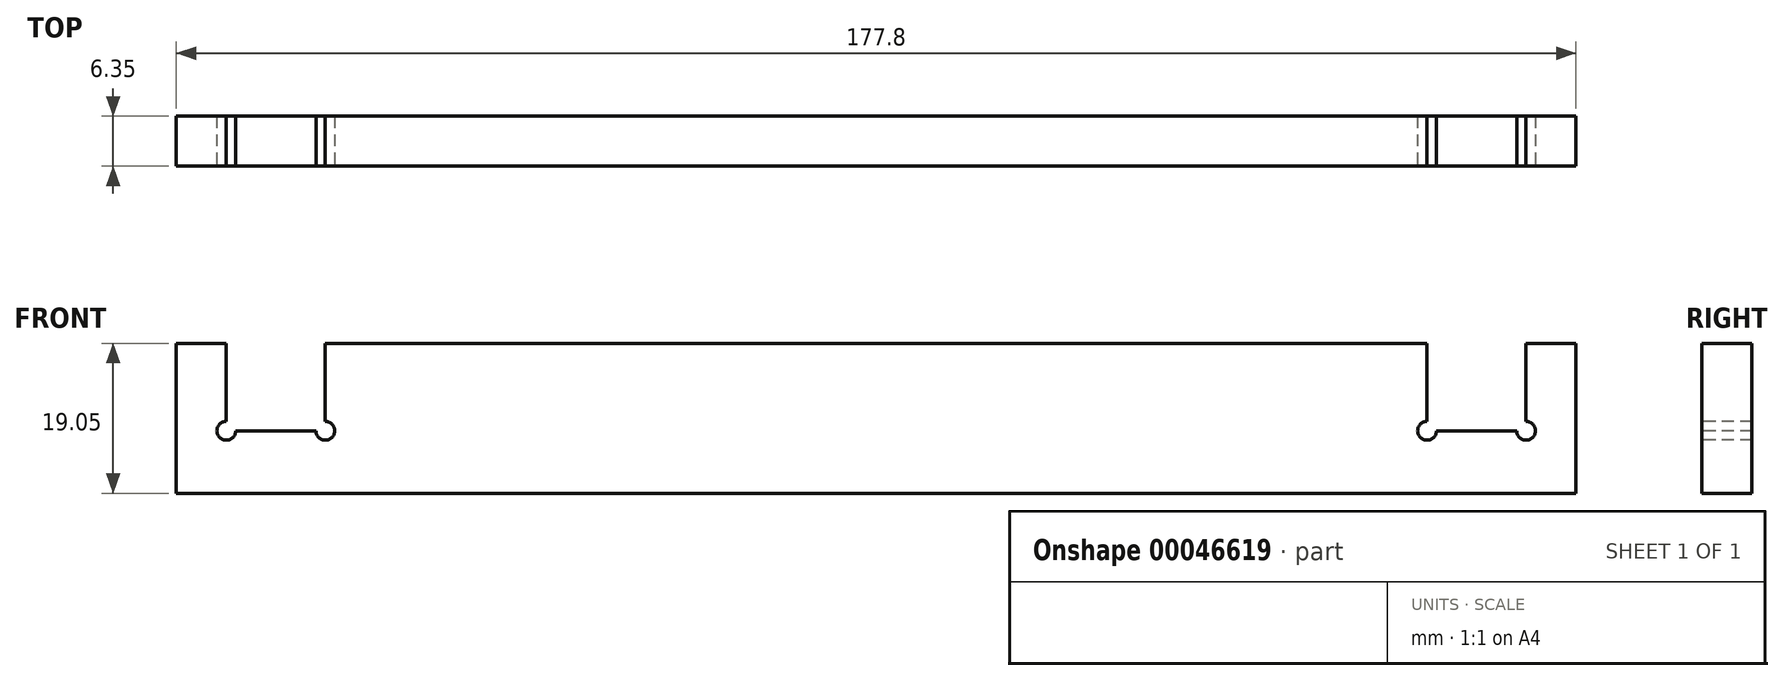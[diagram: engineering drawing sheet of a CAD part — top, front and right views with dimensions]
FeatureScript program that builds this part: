
annotation { "Feature Type Name" : "Feature", "Feature Type Description" : "" }
export const myFeature = defineFeature(function(context is Context, id is Id, definition is map)
    precondition{}
    {
        {
            var Q0;
            Q0=qCreatedBy(makeId("Top.planeOp"),FACE);
            var sketch = newSketch(context, id + "F0", { "sketchPlane" : qUnion([Q0])});
            skLineSegment(sketch, "E0.rect.bottom", {"start": v(-88.9, -3.18) * mm, "end": v(88.9, -3.18) * mm});
            skLineSegment(sketch, "E0.rect.top", {"start": v(-88.9, 3.18) * mm, "end": v(88.9, 3.18) * mm});
            skLineSegment(sketch, "E0.rect.left", {"start": v(-88.9, -3.18) * mm, "end": v(-88.9, 3.18) * mm});
            skLineSegment(sketch, "E0.rect.right", {"start": v(88.9, -3.18) * mm, "end": v(88.9, 3.18) * mm});
            skPoint(sketch, "E0.rect.middle", {"position": v(0, 0) * mm});
            skSolve(sketch);
        }
        {
            var Q0;
            Q0=makeQuery(id+"F0.imprint","IMPRINT",FACE,{"disambiguationData":[TD([[makeQuery(id+"F0.imprint","IMPRINT",EDGE,{"derivedFrom":sQuery(id+"F0.wireOp",EDGE,"E0.rect.bottom")}),1.0]])]});
            extrude(context, id + "F1", {"entities" : qUnion([Q0]), "depth" : 19.05 * mm});
        }
        {
            var Q0;
            Q0=makeQuery(id+"F1.opExtrude","SWEPT_FACE",FACE,{"disambiguationData":[OSD([sQuery(id+"F0.wireOp",EDGE,"E0.rect.bottom")])]});
            var sketch = newSketch(context, id + "F2", { "sketchPlane" : qUnion([Q0])});
            skLineSegment(sketch, "E1.bottom", {"start": v(-82.55, 19.05) * mm, "end": v(-69.98, 19.05) * mm});
            skLineSegment(sketch, "E1.top", {"start": v(-82.55, 7.94) * mm, "end": v(-69.98, 7.94) * mm});
            skLineSegment(sketch, "E1.left", {"start": v(-82.55, 19.05) * mm, "end": v(-82.55, 7.94) * mm});
            skLineSegment(sketch, "E1.right", {"start": v(-69.98, 19.05) * mm, "end": v(-69.98, 7.94) * mm});
            skLineSegment(sketch, "E2", {"start": v(0, 19.05) * mm, "end": v(0, 0) * mm, "construction": true});
            skLineSegment(sketch, "E3.MirrorCS", {"start": v(69.98, 19.05) * mm, "end": v(69.98, 7.94) * mm});
            skLineSegment(sketch, "E4.MirrorCS", {"start": v(82.55, 7.94) * mm, "end": v(69.98, 7.94) * mm});
            skLineSegment(sketch, "E5.MirrorCS", {"start": v(82.55, 19.05) * mm, "end": v(82.55, 7.94) * mm});
            skLineSegment(sketch, "E6.MirrorCS", {"start": v(82.55, 19.05) * mm, "end": v(69.98, 19.05) * mm});
            skCircle(sketch, "E7", {"center": v(-82.55, 7.94) * mm, "radius": 1.2 * mm});
            skCircle(sketch, "E8", {"center": v(-69.98, 7.94) * mm, "radius": 1.2 * mm});
            skCircle(sketch, "E9.MirrorC", {"center": v(82.55, 7.94) * mm, "radius": 1.2 * mm});
            skCircle(sketch, "E10.MirrorC", {"center": v(69.98, 7.94) * mm, "radius": 1.2 * mm});
            skSolve(sketch);
        }
        {
            var Q0;
            {var subQ0=sQuery(id+"F2.wireOp",EDGE,"E1.bottom");Q0=makeQuery(id+"F2.imprint","IMPRINT",FACE,{"disambiguationData":[TD([[makeQuery(id+"F2.imprint","IMPRINT",EDGE,{"derivedFrom":subQ0}),-1.0]])]});}
            var Q1;
            {var subQ1=sQuery(id+"F2.wireOp",EDGE,"E1.left");var subQ3=sQuery(id+"F2.wireOp",EDGE,"E1.top");var subQ5=makeQuery(id+"F2.imprint","INTERSECT",VERTEX,{"derivedFrom":[subQ3,subQ1]});Q1=makeQuery(id+"F2.imprint","IMPRINT",FACE,{"disambiguationData":[TD([[makeQuery(id+"F2.imprint","IMPRINT",EDGE,{"disambiguationData":[TD([[subQ5,-1.0]])],"derivedFrom":subQ3}),-1.0]])]});}
            var Q2;
            {var subQ0=sQuery(id+"F2.wireOp",EDGE,"E1.left");var subQ3=sQuery(id+"F2.wireOp",EDGE,"E1.top");var subQ4=makeQuery(id+"F2.imprint","INTERSECT",VERTEX,{"derivedFrom":[subQ3,subQ0]});Q2=makeQuery(id+"F2.imprint","IMPRINT",FACE,{"disambiguationData":[TD([[makeQuery(id+"F2.imprint","IMPRINT",EDGE,{"disambiguationData":[TD([[subQ4,-1.0]])],"derivedFrom":subQ3}),1.0]])]});}
            var Q3;
            {var subQ0=sQuery(id+"F2.wireOp",EDGE,"E1.right");var subQ3=sQuery(id+"F2.wireOp",EDGE,"E1.top");var subQ4=makeQuery(id+"F2.imprint","INTERSECT",VERTEX,{"derivedFrom":[subQ3,subQ0]});Q3=makeQuery(id+"F2.imprint","IMPRINT",FACE,{"disambiguationData":[TD([[makeQuery(id+"F2.imprint","IMPRINT",EDGE,{"disambiguationData":[TD([[subQ4,1.0]])],"derivedFrom":subQ3}),1.0]])]});}
            var Q4;
            {var subQ1=sQuery(id+"F2.wireOp",EDGE,"E1.right");var subQ3=sQuery(id+"F2.wireOp",EDGE,"E1.top");var subQ5=makeQuery(id+"F2.imprint","INTERSECT",VERTEX,{"derivedFrom":[subQ3,subQ1]});Q4=makeQuery(id+"F2.imprint","IMPRINT",FACE,{"disambiguationData":[TD([[makeQuery(id+"F2.imprint","IMPRINT",EDGE,{"disambiguationData":[TD([[subQ5,1.0]])],"derivedFrom":subQ3}),-1.0]])]});}
            var Q5;
            {var subQ10=sQuery(id+"F2.wireOp",EDGE,"E6.MirrorCS");Q5=makeQuery(id+"F2.imprint","IMPRINT",FACE,{"disambiguationData":[TD([[makeQuery(id+"F2.imprint","IMPRINT",EDGE,{"derivedFrom":subQ10}),-1.0]])]});}
            var Q6;
            {var subQ1=sQuery(id+"F2.wireOp",EDGE,"E4.MirrorCS");var subQ3=sQuery(id+"F2.wireOp",EDGE,"E3.MirrorCS");var subQ5=makeQuery(id+"F2.imprint","INTERSECT",VERTEX,{"derivedFrom":[subQ3,subQ1]});Q6=makeQuery(id+"F2.imprint","IMPRINT",FACE,{"disambiguationData":[TD([[makeQuery(id+"F2.imprint","IMPRINT",EDGE,{"disambiguationData":[TD([[subQ5,1.0]])],"derivedFrom":subQ3}),-1.0]])]});}
            var Q7;
            {var subQ1=sQuery(id+"F2.wireOp",EDGE,"E4.MirrorCS");var subQ3=sQuery(id+"F2.wireOp",EDGE,"E3.MirrorCS");var subQ5=makeQuery(id+"F2.imprint","INTERSECT",VERTEX,{"derivedFrom":[subQ3,subQ1]});Q7=makeQuery(id+"F2.imprint","IMPRINT",FACE,{"disambiguationData":[TD([[makeQuery(id+"F2.imprint","IMPRINT",EDGE,{"disambiguationData":[TD([[subQ5,1.0]])],"derivedFrom":subQ3}),1.0]])]});}
            var Q8;
            {var subQ1=sQuery(id+"F2.wireOp",EDGE,"E5.MirrorCS");var subQ3=sQuery(id+"F2.wireOp",EDGE,"E4.MirrorCS");var subQ5=makeQuery(id+"F2.imprint","INTERSECT",VERTEX,{"derivedFrom":[subQ3,subQ1]});Q8=makeQuery(id+"F2.imprint","IMPRINT",FACE,{"disambiguationData":[TD([[makeQuery(id+"F2.imprint","IMPRINT",EDGE,{"disambiguationData":[TD([[subQ5,-1.0]])],"derivedFrom":subQ3}),-1.0]])]});}
            var Q9;
            {var subQ1=sQuery(id+"F2.wireOp",EDGE,"E5.MirrorCS");var subQ3=sQuery(id+"F2.wireOp",EDGE,"E4.MirrorCS");var subQ5=makeQuery(id+"F2.imprint","INTERSECT",VERTEX,{"derivedFrom":[subQ3,subQ1]});Q9=makeQuery(id+"F2.imprint","IMPRINT",FACE,{"disambiguationData":[TD([[makeQuery(id+"F2.imprint","IMPRINT",EDGE,{"disambiguationData":[TD([[subQ5,-1.0]])],"derivedFrom":subQ3}),1.0]])]});}
            extrude(context, id + "F3", {"entities" : qUnion([Q0, Q1, Q2, Q3, Q4, Q5, Q6, Q7, Q8, Q9]), "operationType" : NewBodyOperationType.REMOVE, "endBound" : BoundingType.UP_TO_NEXT, "oppositeDirection" : true, "depth" : 25.4 * mm});
        }
    });
